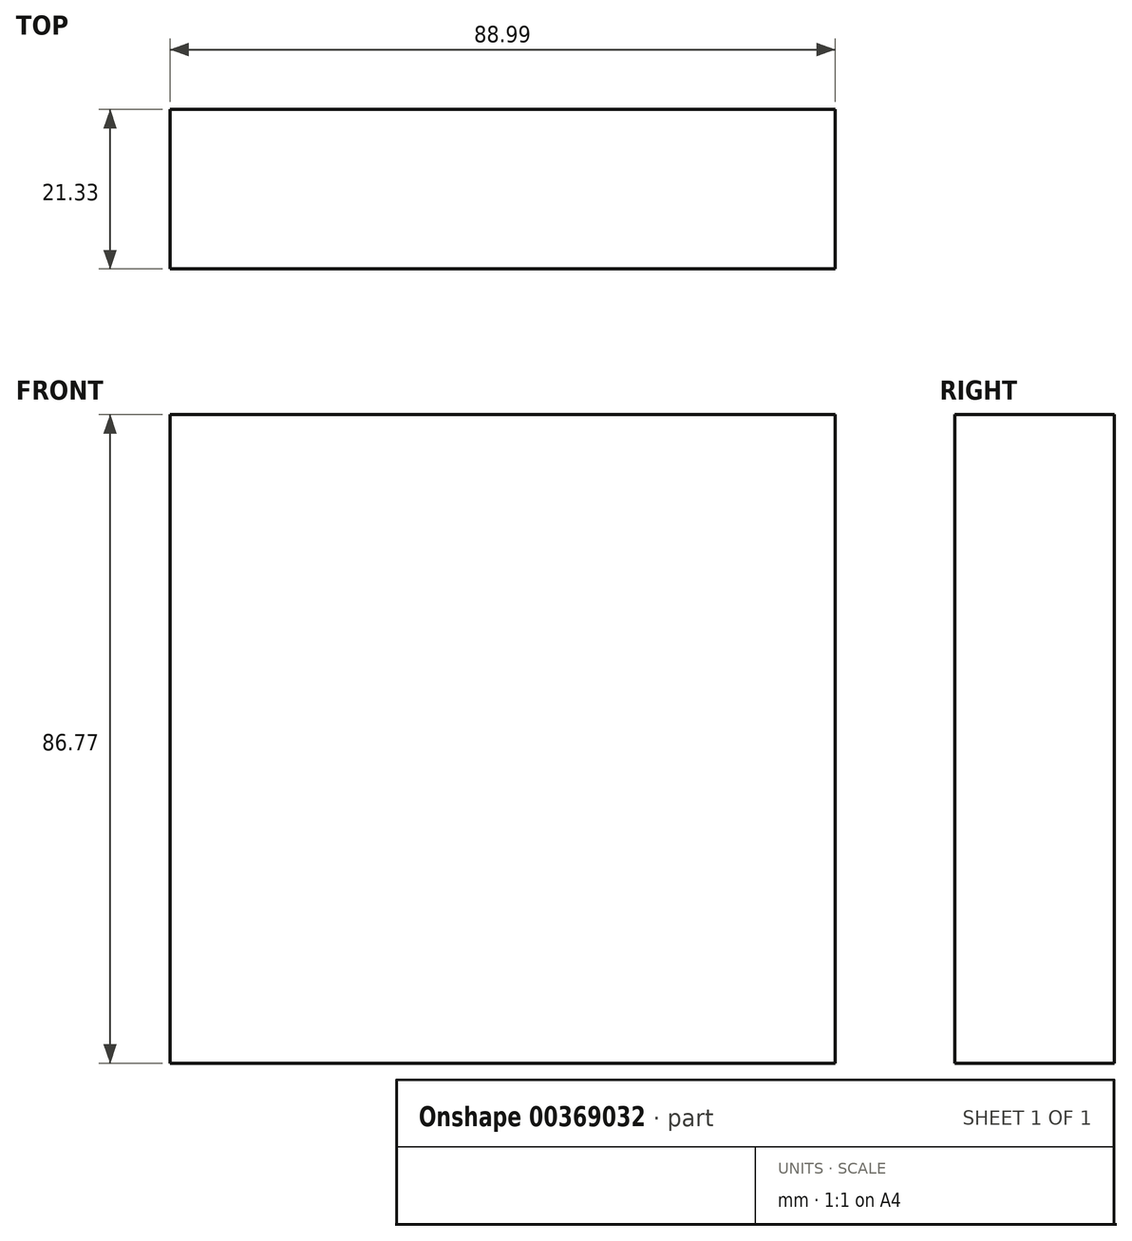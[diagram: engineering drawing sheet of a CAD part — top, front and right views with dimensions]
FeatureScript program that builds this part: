
annotation { "Feature Type Name" : "Feature", "Feature Type Description" : "" }
export const myFeature = defineFeature(function(context is Context, id is Id, definition is map)
    precondition{}
    {
        {
            var Q0;
            Q0=qCreatedBy(makeId("Front.planeOp"),FACE);
            var sketch = newSketch(context, id + "F0", { "sketchPlane" : qUnion([Q0])});
            skLineSegment(sketch, "E0.bottom", {"start": v(-42.28, 41.55) * mm, "end": v(46.7, 41.55) * mm});
            skLineSegment(sketch, "E0.top", {"start": v(-42.28, -45.22) * mm, "end": v(46.7, -45.22) * mm});
            skLineSegment(sketch, "E0.left", {"start": v(-42.28, 41.55) * mm, "end": v(-42.28, -45.22) * mm});
            skLineSegment(sketch, "E0.right", {"start": v(46.7, 41.55) * mm, "end": v(46.7, -45.22) * mm});
            skSolve(sketch);
        }
        {
            var Q0;
            Q0=makeQuery(id+"F0.imprint","IMPRINT",FACE,{"disambiguationData":[TD([[makeQuery(id+"F0.imprint","IMPRINT",EDGE,{"derivedFrom":sQuery(id+"F0.wireOp",EDGE,"E0.bottom")}),-1.0]])]});
            var sketch = newSketch(context, id + "F1", { "sketchPlane" : qUnion([Q0])});
            skSolve(sketch);
        }
        {
            var Q0;
            Q0=makeQuery(id+"F1.imprint","IMPRINT",FACE,{"disambiguationData":[TD([[makeQuery(id+"F1.imprint","IMPRINT",EDGE,{"derivedFrom":makeQuery(id+"F0.imprint","IMPRINT",EDGE,{"derivedFrom":sQuery(id+"F0.wireOp",EDGE,"E0.bottom")})}),-1.0]])]});
            extrude(context, id + "F2", {"entities" : qUnion([Q0]), "depth" : 21.33 * mm});
        }
    });
